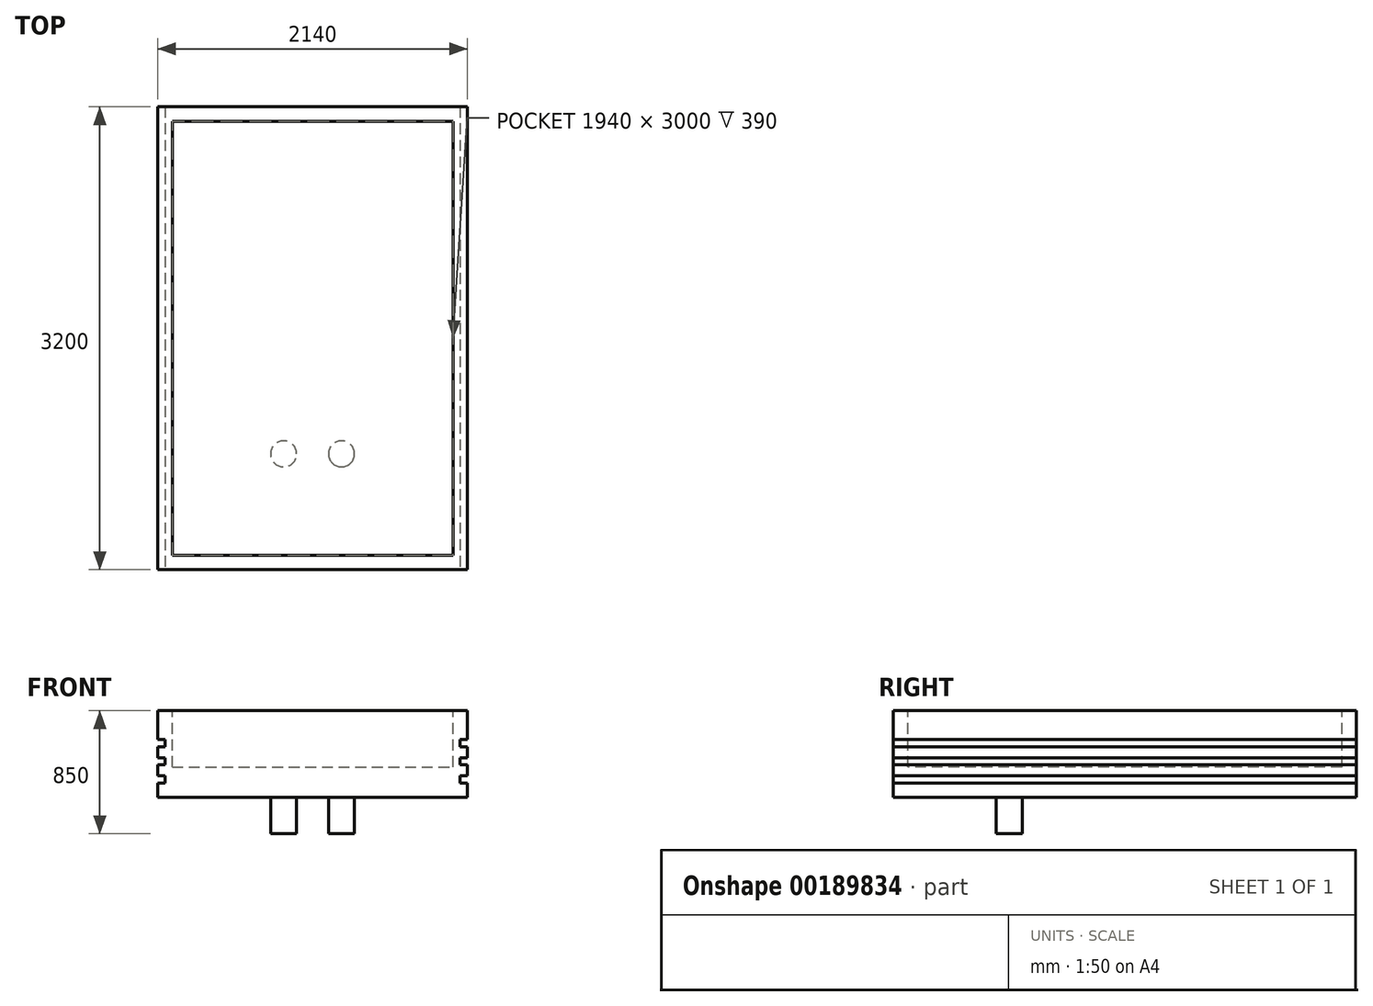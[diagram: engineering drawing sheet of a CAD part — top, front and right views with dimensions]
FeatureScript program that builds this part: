
annotation { "Feature Type Name" : "Feature", "Feature Type Description" : "" }
export const myFeature = defineFeature(function(context is Context, id is Id, definition is map)
    precondition{}
    {
        {
            var Q0;
            Q0=qCreatedBy(makeId("Front.planeOp"),FACE);
            var sketch = newSketch(context, id + "F0", { "sketchPlane" : qUnion([Q0])});
            skLineSegment(sketch, "E0.bottom", {"start": v(-1070, 0) * mm, "end": v(1070, 0) * mm});
            skLineSegment(sketch, "E0.top", {"start": v(-1070, 600) * mm, "end": v(1070, 600) * mm});
            skLineSegment(sketch, "E0.left", {"start": v(-1070, 0) * mm, "end": v(-1070, 600) * mm});
            skLineSegment(sketch, "E0.right", {"start": v(1070, 0) * mm, "end": v(1070, 600) * mm});
            skSolve(sketch);
        }
        {
            var Q0;
            Q0=makeQuery(id+"F0.imprint","IMPRINT",FACE,{"disambiguationData":[TD([[makeQuery(id+"F0.imprint","IMPRINT",EDGE,{"derivedFrom":sQuery(id+"F0.wireOp",EDGE,"E0.bottom")}),1.0]])]});
            extrude(context, id + "F1", {"entities" : qUnion([Q0]), "depth" : 3200 * mm});
        }
        {
            var Q0;
            Q0=makeQuery(id+"F1.opExtrude","SWEPT_FACE",FACE,{"disambiguationData":[OSD([sQuery(id+"F0.wireOp",EDGE,"E0.top")])]});
            var sketch = newSketch(context, id + "F2", { "sketchPlane" : qUnion([Q0])});
            skLineSegment(sketch, "E1.bottom", {"start": v(-970, -100) * mm, "end": v(970, -100) * mm});
            skLineSegment(sketch, "E1.top", {"start": v(-970, -3100) * mm, "end": v(970, -3100) * mm});
            skLineSegment(sketch, "E1.left", {"start": v(-970, -100) * mm, "end": v(-970, -3100) * mm});
            skLineSegment(sketch, "E1.right", {"start": v(970, -100) * mm, "end": v(970, -3100) * mm});
            skSolve(sketch);
        }
        {
            var Q0;
            Q0=makeQuery(id+"F2.imprint","IMPRINT",FACE,{"disambiguationData":[TD([[makeQuery(id+"F2.imprint","IMPRINT",EDGE,{"derivedFrom":sQuery(id+"F2.wireOp",EDGE,"E1.bottom")}),-1.0]])]});
            extrude(context, id + "F3", {"entities" : qUnion([Q0]), "operationType" : NewBodyOperationType.REMOVE, "oppositeDirection" : true, "depth" : 390 * mm});
        }
        {
            var Q0;
            Q0=makeQuery(id+"F1.opExtrude","SWEPT_FACE",FACE,{"disambiguationData":[OSD([sQuery(id+"F0.wireOp",EDGE,"E0.bottom")])]});
            var sketch = newSketch(context, id + "F4", { "sketchPlane" : qUnion([Q0])});
            skCircle(sketch, "E2", {"center": v(-200, 2400) * mm, "radius": 90 * mm});
            skCircle(sketch, "E3", {"center": v(200, 2400) * mm, "radius": 90 * mm});
            skLineSegment(sketch, "E4", {"start": v(0, 3200) * mm, "end": v(0, 0) * mm, "construction": true});
            skSolve(sketch);
        }
        {
            var Q0;
            Q0=makeQuery(id+"F4.imprint","IMPRINT",FACE,{"disambiguationData":[TD([[makeQuery(id+"F4.imprint","IMPRINT",EDGE,{"derivedFrom":sQuery(id+"F4.wireOp",EDGE,"E2")}),1.0]])]});
            var Q1;
            Q1=makeQuery(id+"F4.imprint","IMPRINT",FACE,{"disambiguationData":[TD([[makeQuery(id+"F4.imprint","IMPRINT",EDGE,{"derivedFrom":sQuery(id+"F4.wireOp",EDGE,"E3")}),1.0]])]});
            extrude(context, id + "F5", {"entities" : qUnion([Q0, Q1]), "operationType" : NewBodyOperationType.ADD, "depth" : 250 * mm});
        }
        {
            var Q0;
            Q0=makeQuery(id+"F1.opExtrude","CAP_FACE",FACE,{"disambiguationData":[OSD([sQuery(id+"F0.wireOp",EDGE,"E0.bottom"),sQuery(id+"F0.wireOp",EDGE,"E0.top"),sQuery(id+"F0.wireOp",EDGE,"E0.left"),sQuery(id+"F0.wireOp",EDGE,"E0.right")])],"isStart":false});
            var sketch = newSketch(context, id + "F6", { "sketchPlane" : qUnion([Q0])});
            skLineSegment(sketch, "E5.bottom", {"start": v(1070, 400) * mm, "end": v(1020, 400) * mm});
            skLineSegment(sketch, "E5.top", {"start": v(1070, 350) * mm, "end": v(1020, 350) * mm});
            skLineSegment(sketch, "E5.left", {"start": v(1070, 400) * mm, "end": v(1070, 350) * mm});
            skLineSegment(sketch, "E5.right", {"start": v(1020, 400) * mm, "end": v(1020, 350) * mm});
            skLineSegment(sketch, "E6.bottom", {"start": v(1070, 275) * mm, "end": v(1020, 275) * mm});
            skLineSegment(sketch, "E6.top", {"start": v(1070, 225) * mm, "end": v(1020, 225) * mm});
            skLineSegment(sketch, "E6.left", {"start": v(1070, 275) * mm, "end": v(1070, 225) * mm});
            skLineSegment(sketch, "E6.right", {"start": v(1020, 275) * mm, "end": v(1020, 225) * mm});
            skLineSegment(sketch, "E7.bottom", {"start": v(1070, 150) * mm, "end": v(1020, 150) * mm});
            skLineSegment(sketch, "E7.top", {"start": v(1070, 100) * mm, "end": v(1020, 100) * mm});
            skLineSegment(sketch, "E7.left", {"start": v(1070, 150) * mm, "end": v(1070, 100) * mm});
            skLineSegment(sketch, "E7.right", {"start": v(1020, 150) * mm, "end": v(1020, 100) * mm});
            skLineSegment(sketch, "E8.bottom", {"start": v(-1070, 400) * mm, "end": v(-1020, 400) * mm});
            skLineSegment(sketch, "E8.top", {"start": v(-1070, 350) * mm, "end": v(-1020, 350) * mm});
            skLineSegment(sketch, "E8.left", {"start": v(-1070, 400) * mm, "end": v(-1070, 350) * mm});
            skLineSegment(sketch, "E8.right", {"start": v(-1020, 400) * mm, "end": v(-1020, 350) * mm});
            skLineSegment(sketch, "E9.bottom", {"start": v(-1070, 275) * mm, "end": v(-1020, 275) * mm});
            skLineSegment(sketch, "E9.top", {"start": v(-1070, 225) * mm, "end": v(-1020, 225) * mm});
            skLineSegment(sketch, "E9.left", {"start": v(-1070, 275) * mm, "end": v(-1070, 225) * mm});
            skLineSegment(sketch, "E9.right", {"start": v(-1020, 275) * mm, "end": v(-1020, 225) * mm});
            skLineSegment(sketch, "E10.bottom", {"start": v(-1070, 150) * mm, "end": v(-1020, 150) * mm});
            skLineSegment(sketch, "E10.top", {"start": v(-1070, 100) * mm, "end": v(-1020, 100) * mm});
            skLineSegment(sketch, "E10.left", {"start": v(-1070, 150) * mm, "end": v(-1070, 100) * mm});
            skLineSegment(sketch, "E10.right", {"start": v(-1020, 150) * mm, "end": v(-1020, 100) * mm});
            skSolve(sketch);
        }
        {
            var Q0;
            Q0=makeQuery(id+"F6.imprint","IMPRINT",FACE,{"disambiguationData":[TD([[makeQuery(id+"F6.imprint","IMPRINT",EDGE,{"derivedFrom":sQuery(id+"F6.wireOp",EDGE,"E5.bottom")}),1.0]])]});
            var Q1;
            Q1=makeQuery(id+"F6.imprint","IMPRINT",FACE,{"disambiguationData":[TD([[makeQuery(id+"F6.imprint","IMPRINT",EDGE,{"derivedFrom":sQuery(id+"F6.wireOp",EDGE,"E6.bottom")}),1.0]])]});
            var Q2;
            Q2=makeQuery(id+"F6.imprint","IMPRINT",FACE,{"disambiguationData":[TD([[makeQuery(id+"F6.imprint","IMPRINT",EDGE,{"derivedFrom":sQuery(id+"F6.wireOp",EDGE,"E7.bottom")}),1.0]])]});
            var Q3;
            Q3=makeQuery(id+"F6.imprint","IMPRINT",FACE,{"disambiguationData":[TD([[makeQuery(id+"F6.imprint","IMPRINT",EDGE,{"derivedFrom":sQuery(id+"F6.wireOp",EDGE,"E10.bottom")}),-1.0]])]});
            var Q4;
            Q4=makeQuery(id+"F6.imprint","IMPRINT",FACE,{"disambiguationData":[TD([[makeQuery(id+"F6.imprint","IMPRINT",EDGE,{"derivedFrom":sQuery(id+"F6.wireOp",EDGE,"E9.bottom")}),-1.0]])]});
            var Q5;
            Q5=makeQuery(id+"F6.imprint","IMPRINT",FACE,{"disambiguationData":[TD([[makeQuery(id+"F6.imprint","IMPRINT",EDGE,{"derivedFrom":sQuery(id+"F6.wireOp",EDGE,"E8.bottom")}),-1.0]])]});
            extrude(context, id + "F7", {"entities" : qUnion([Q0, Q1, Q2, Q3, Q4, Q5]), "operationType" : NewBodyOperationType.REMOVE, "oppositeDirection" : true, "depth" : 3200 * mm});
        }
    });
